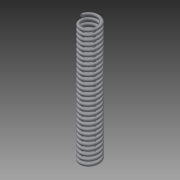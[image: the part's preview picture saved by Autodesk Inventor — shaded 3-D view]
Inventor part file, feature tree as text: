
AUTODESK INVENTOR PART (.ipt)
format: ipt  version: 2014 SP1 (Build 180222100, 222)  size: 438,272 bytes
history: native  units: in
note: dims shown in document units (in); Inventor stores cm internally (conversion verified against a paired STEP export)
features: other x1, helix x1, sketch x1
ambient origin geometry x8: Origin, YZ Plane, XZ Plane, XY Plane, X Axis, Y Axis, Z Axis, Center Point
bodies: Solid1 (feature_tree)
feature tree (3):
  other  "Small Mainspring"
  helix  "Coil1"  [1 undecoded]
  sketch  "Sketch1"  dims[d1=0.171in d2=1.068in d3=1.043in d4=1.0in d5=1.043in d6=11.0236in d7=0.0in d8=90.0deg d9=90.0deg d10=90.0deg d11=90.0deg]
note: 1 required parameter value undecoded (feature->parameter linkage not recoverable at this tier; creation-order binding heuristic only, values carry confidence <= 0.55)
